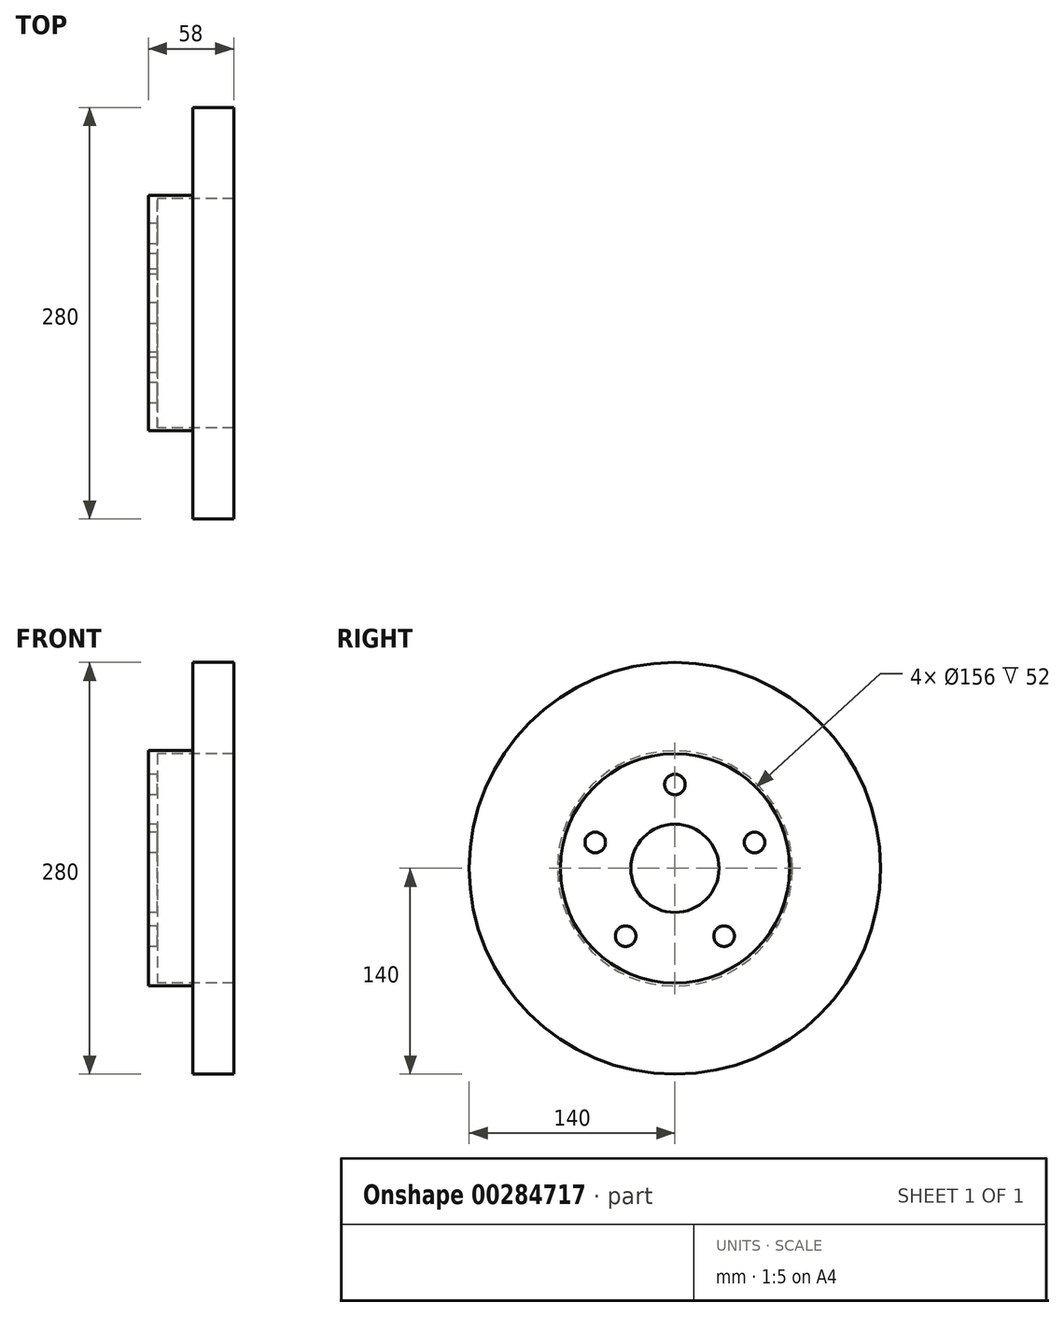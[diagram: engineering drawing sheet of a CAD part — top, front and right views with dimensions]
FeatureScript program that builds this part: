
annotation { "Feature Type Name" : "Feature", "Feature Type Description" : "" }
export const myFeature = defineFeature(function(context is Context, id is Id, definition is map)
    precondition{}
    {
        {
            var Q0;
            Q0=qCreatedBy(makeId("Front.planeOp"),FACE);
            var sketch = newSketch(context, id + "F0", { "sketchPlane" : qUnion([Q0])});
            skLineSegment(sketch, "E0", {"start": v(0, 0) * mm, "end": v(0, 140) * mm});
            skLineSegment(sketch, "E1", {"start": v(0, 140) * mm, "end": v(-28, 140) * mm});
            skPoint(sketch, "E2", {"position": v(0, 80) * mm});
            skLineSegment(sketch, "E3", {"start": v(-139.6, 80) * mm, "end": v(163.16, 80) * mm, "construction": true});
            skLineSegment(sketch, "E4", {"start": v(-28, 140) * mm, "end": v(-28, 80) * mm});
            skLineSegment(sketch, "E5", {"start": v(-28, 80) * mm, "end": v(0, 80) * mm});
            skLineSegment(sketch, "E6", {"start": v(-28, 80) * mm, "end": v(-58, 80) * mm});
            skLineSegment(sketch, "E7", {"start": v(-58, 80) * mm, "end": v(-58, 0) * mm});
            skLineSegment(sketch, "E8", {"start": v(-58, 0) * mm, "end": v(0, 0) * mm, "construction": true});
            skLineSegment(sketch, "E9.0", {"start": v(-52, 80) * mm, "end": v(-52, 0) * mm});
            skLineSegment(sketch, "E10", {"start": v(-58, 0) * mm, "end": v(-52, 0) * mm, "construction": true});
            skLineSegment(sketch, "E11", {"start": v(-58, 0) * mm, "end": v(-52, 0) * mm});
            skLineSegment(sketch, "E12", {"start": v(0, 80) * mm, "end": v(0, 78) * mm});
            skLineSegment(sketch, "E13", {"start": v(0, 78) * mm, "end": v(-52, 78) * mm});
            skSolve(sketch);
        }
        {
            var Q0;
            Q0=qSketchRegion(id+"F0",true);
            var Q1;
            Q1=sQuery(id+"F0.wireOp",EDGE,"E8");
            revolve(context, id + "F1", {"entities" : qUnion([Q0]), "axis" : qUnion([Q1]), "revolveType" : RevolveType.FULL});
        }
        {
            var Q0;
            Q0=qCreatedBy(makeId("Right.planeOp"),FACE);
            cPlane(context, id + "F2", {"entities" : qUnion([Q0]), "cplaneType" : CPlaneType.OFFSET, "offset" : 58 * mm, "oppositeDirection" : true, "width" : 150 * mm, "height" : 150 * mm});
        }
        {
            var Q0;
            Q0=qCreatedBy(id+"F2.planeOp",FACE);
            var sketch = newSketch(context, id + "F3", { "sketchPlane" : qUnion([Q0])});
            skCircle(sketch, "E14", {"center": v(0, 0) * mm, "radius": 30 * mm});
            skPoint(sketch, "E15", {"position": v(0, 57) * mm});
            skCircle(sketch, "E16", {"center": v(0, 57) * mm, "radius": 7 * mm});
            skSolve(sketch);
        }
        {
            var Q0;
            Q0=qSketchRegion(id+"F3",true);
            extrude(context, id + "F4", {"entities" : qUnion([Q0]), "operationType" : NewBodyOperationType.REMOVE, "depth" : 7 * mm});
        }
        {
            var Q0;
            Q0=makeQuery(id+"F4.boolean.opBoolean","COPY",FACE,{"derivedFrom":makeQuery(id+"F4.opExtrude","SWEPT_FACE",FACE,{"disambiguationData":[OSD([sQuery(id+"F3.wireOp",EDGE,"E16")])]})});
            var Q1;
            Q1=makeQuery(id+"F1.opRevolve","SWEPT_EDGE",EDGE,{"disambiguationData":[OSD([sQuery(id+"F0.wireOp",EDGE,"E6"),sQuery(id+"F0.wireOp",EDGE,"E7")])]});
            circularPattern(context, id + "F5", {"patternType" : PatternType.FACE, "faces" : qUnion([Q0]), "axis" : qUnion([Q1]), "angle" : 360 * degree, "instanceCount" : 5, "equalSpace" : true});
        }
    });
